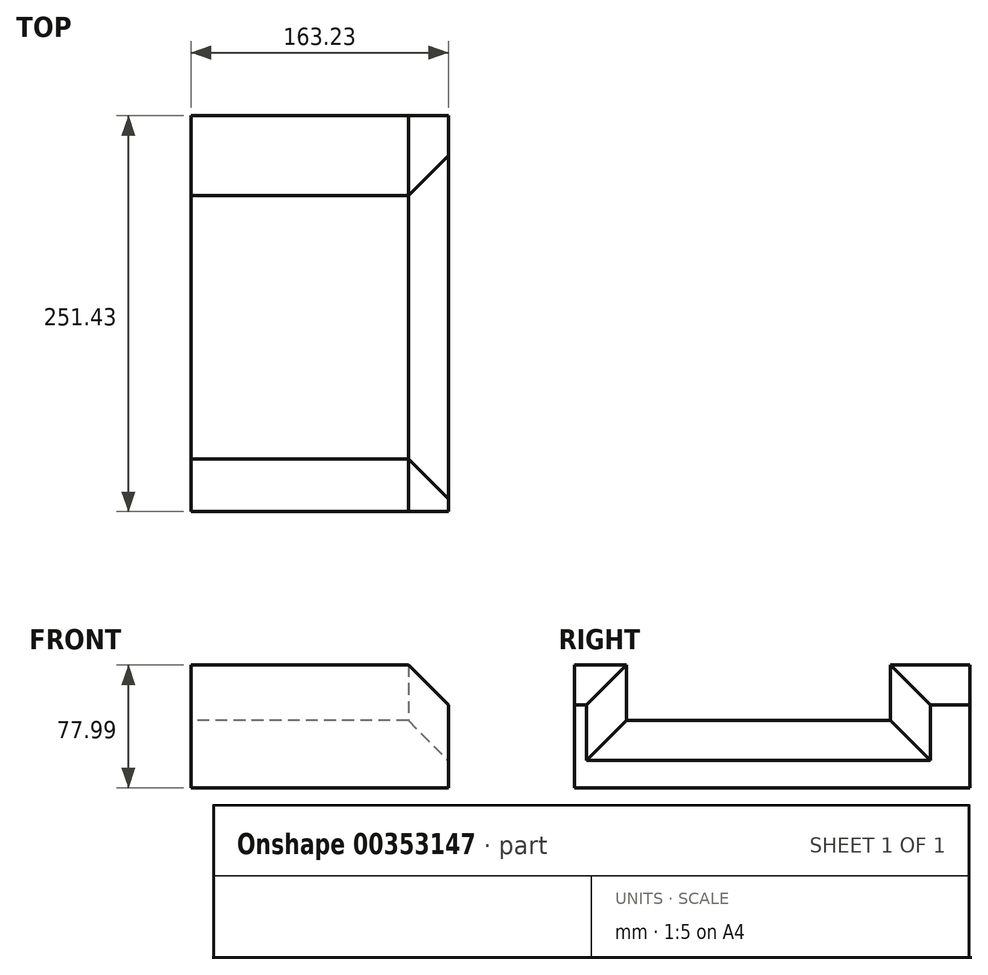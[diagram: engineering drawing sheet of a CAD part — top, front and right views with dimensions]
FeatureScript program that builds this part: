
annotation { "Feature Type Name" : "Feature", "Feature Type Description" : "" }
export const myFeature = defineFeature(function(context is Context, id is Id, definition is map)
    precondition{}
    {
        {
            var Q0;
            Q0=qCreatedBy(makeId("Right.planeOp"),FACE);
            var sketch = newSketch(context, id + "F0", { "sketchPlane" : qUnion([Q0])});
            skLineSegment(sketch, "E0.bottom", {"start": v(-81.03, 0) * mm, "end": v(86.47, 0) * mm});
            skLineSegment(sketch, "E0.top", {"start": v(-81.03, -87.78) * mm, "end": v(86.47, -87.78) * mm});
            skLineSegment(sketch, "E0.left", {"start": v(-81.03, 0) * mm, "end": v(-81.03, -87.78) * mm});
            skLineSegment(sketch, "E0.right", {"start": v(86.47, 0) * mm, "end": v(86.47, -87.78) * mm});
            skLineSegment(sketch, "E1.bottom", {"start": v(137.1, -52.52) * mm, "end": v(-114.32, -52.52) * mm});
            skLineSegment(sketch, "E1.top", {"start": v(137.1, -130.51) * mm, "end": v(-114.32, -130.51) * mm});
            skLineSegment(sketch, "E1.left", {"start": v(137.1, -52.52) * mm, "end": v(137.1, -130.51) * mm});
            skLineSegment(sketch, "E1.right", {"start": v(-114.32, -52.52) * mm, "end": v(-114.32, -130.51) * mm});
            skSolve(sketch);
        }
        {
            var Q0;
            {var subQ1=sQuery(id+"F0.wireOp",EDGE,"E0.top");Q0=makeQuery(id+"F0.imprint","IMPRINT",FACE,{"disambiguationData":[TD([[makeQuery(id+"F0.imprint","IMPRINT",EDGE,{"derivedFrom":subQ1}),-1.0]])]});}
            extrude(context, id + "F1", {"entities" : qUnion([Q0]), "depth" : 163.23 * mm});
        }
        {
            var Q0;
            Q0=makeQuery(id+"F1.opExtrude","CAP_EDGE",EDGE,{"disambiguationData":[OSD([sQuery(id+"F0.wireOp",EDGE,"E0.top")])],"isStart":false});
            var Q1;
            Q1=makeQuery(id+"F1.opExtrude","CAP_EDGE",EDGE,{"disambiguationData":[OSD([sQuery(id+"F0.wireOp",EDGE,"E0.left")])],"isStart":false});
            var Q2;
            Q2=makeQuery(id+"F1.opExtrude","CAP_EDGE",EDGE,{"disambiguationData":[OSD([sQuery(id+"F0.wireOp",EDGE,"E0.right")])],"isStart":false});
            var Q3;
            {var subQ0=sQuery(id+"F0.wireOp",EDGE,"E1.bottom");Q3=makeQuery(id+"F1.opExtrude","CAP_EDGE",EDGE,{"disambiguationData":[OSD([subQ0]),TDD([makeQuery(id+"F0.imprint","IMPRINT",EDGE,{"disambiguationData":[TD([[makeQuery(id+"F0.imprint","INTERSECT",VERTEX,{"derivedFrom":[subQ0,sQuery(id+"F0.wireOp",EDGE,"E1.left")]}),-1.0]])],"derivedFrom":subQ0})])],"isStart":false});}
            var Q4;
            {var subQ0=sQuery(id+"F0.wireOp",EDGE,"E1.bottom");Q4=makeQuery(id+"F1.opExtrude","CAP_EDGE",EDGE,{"disambiguationData":[OSD([subQ0]),TDD([makeQuery(id+"F0.imprint","IMPRINT",EDGE,{"disambiguationData":[TD([[makeQuery(id+"F0.imprint","INTERSECT",VERTEX,{"derivedFrom":[subQ0,sQuery(id+"F0.wireOp",EDGE,"E1.right")]}),1.0]])],"derivedFrom":subQ0})])],"isStart":false});}
            chamfer(context, id + "F2", {"entities" : qUnion([Q0, Q1, Q2, Q3, Q4]), "width" : 25.4 * mm, "tangentPropagation" : true});
        }
    });
